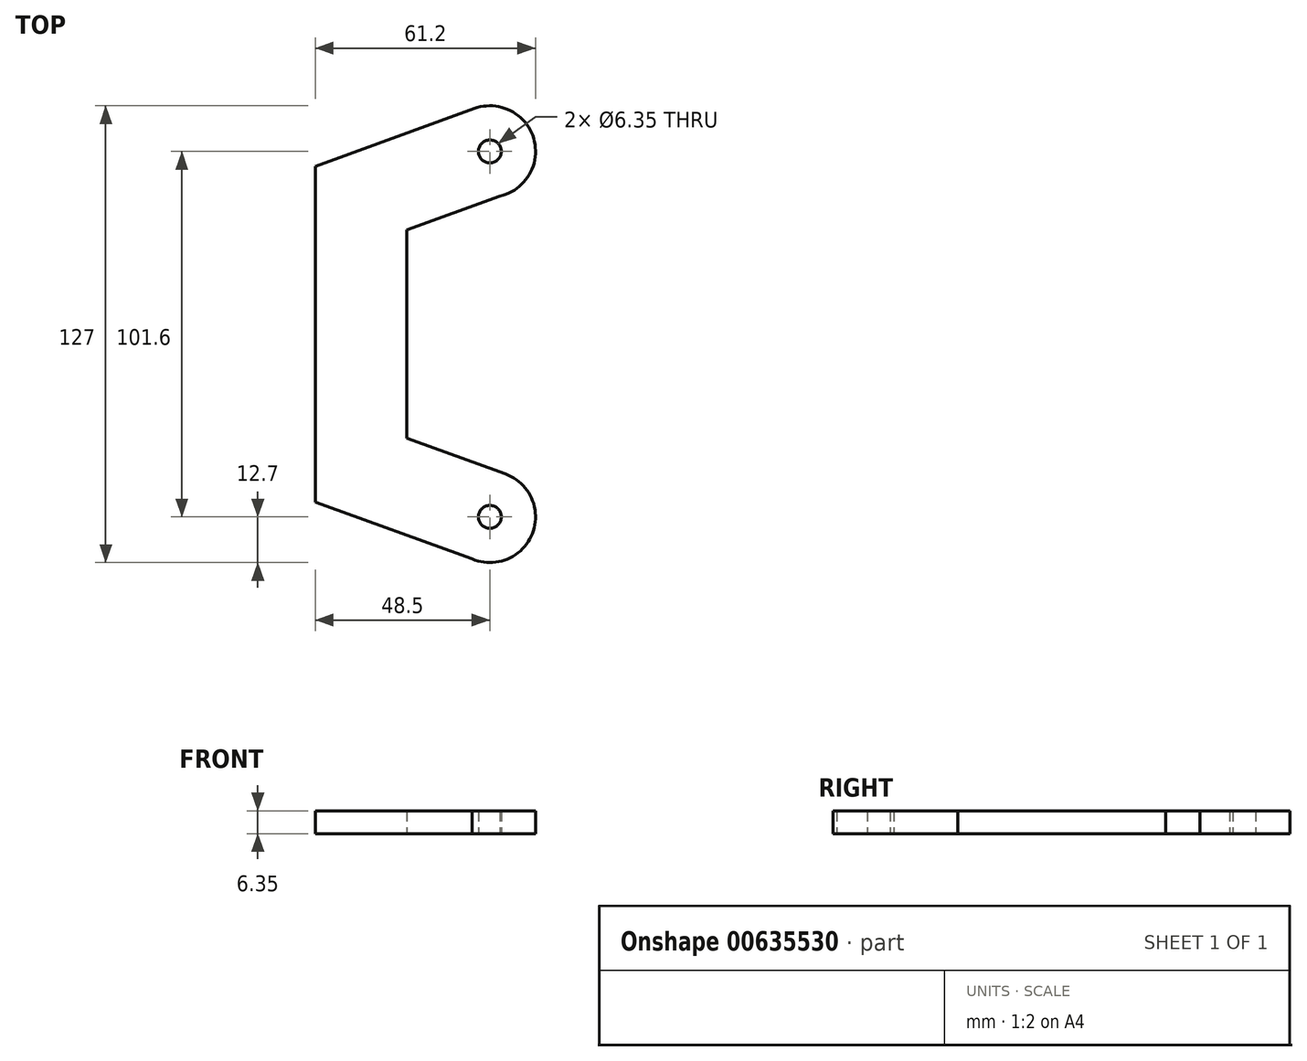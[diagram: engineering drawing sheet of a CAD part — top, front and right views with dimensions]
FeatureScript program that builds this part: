
annotation { "Feature Type Name" : "Feature", "Feature Type Description" : "" }
export const myFeature = defineFeature(function(context is Context, id is Id, definition is map)
    precondition{}
    {
        {
            var Q0;
            Q0=qCreatedBy(makeId("Top.planeOp"),FACE);
            var sketch = newSketch(context, id + "F0", { "sketchPlane" : qUnion([Q0])});
            skCircle(sketch, "E0", {"center": v(0, 0) * mm, "radius": 3.18 * mm});
            skCircle(sketch, "E1", {"center": v(0, 101.6) * mm, "radius": 3.17 * mm});
            skLineSegment(sketch, "E2", {"start": v(0, 0) * mm, "end": v(-35.8, 13.03) * mm});
            skLineSegment(sketch, "E3", {"start": v(-35.8, 13.03) * mm, "end": v(-35.8, 88.57) * mm});
            skLineSegment(sketch, "E4", {"start": v(-35.8, 88.57) * mm, "end": v(0, 101.6) * mm});
            skArc(sketch, "E5", {"start": v(-4.95, -11.7) * mm, "mid": v(11.82, -4.65) * mm, "end": v(4.34, 11.93) * mm});
            skArc(sketch, "E6", {"start": v(2.85, 89.22) * mm, "mid": v(12.18, 105.2) * mm, "end": v(-4.34, 113.53) * mm});
            skLineSegment(sketch, "E7", {"start": v(5.77, 90.29) * mm, "end": v(-23.1, 79.78) * mm});
            skLineSegment(sketch, "E8", {"start": v(-4.34, 113.53) * mm, "end": v(-48.5, 97.46) * mm});
            skLineSegment(sketch, "E9", {"start": v(4.34, 11.93) * mm, "end": v(-23.1, 21.92) * mm});
            skLineSegment(sketch, "E10", {"start": v(-3.72, -12.14) * mm, "end": v(-48.5, 4.16) * mm});
            skLineSegment(sketch, "E11", {"start": v(-48.5, 97.46) * mm, "end": v(-48.5, 4.16) * mm});
            skLineSegment(sketch, "E12", {"start": v(-23.1, 79.78) * mm, "end": v(-23.1, 21.92) * mm});
            skSolve(sketch);
        }
        {
            var Q0;
            Q0 = qSketchRegion(id + "F0", true);
            extrude(context, id + "F1", {"entities" : qUnion([Q0]), "depth" : 6.35 * mm, "offsetDistance" : 25.4 * mm});
        }
    });
